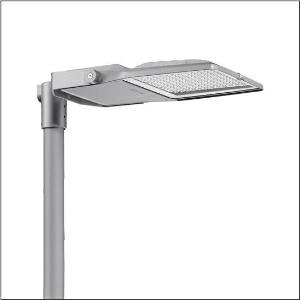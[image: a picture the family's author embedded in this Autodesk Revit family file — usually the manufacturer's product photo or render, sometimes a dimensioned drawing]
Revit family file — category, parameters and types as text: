
# Revit family: floodlight_fl_21_midi___pl64_5xa7785e2e3a_0c5c
name_source: partatom
category: Lighting Fixtures
units: mm (PartAtom-declared; Revit-internal decimal feet)

## family parameters
Cut with Voids When Loaded = No
Host = Face
Light Source = No
Part Type = Normal
Room Calculation Point = No
Round Connector Dimension = Use Diameter
Shared = No

## types (1)
- --- (1 x LED, 26020 lm, 212.4 W, 3000K)
    Apparent Load = 212 VA
    CIE Flux Codes = 28 80 98 100 100
    Color Rendering = 70
    Color Temperature = 3000K
    Default Elevation = 1800 mm
    Description = Floodlight FL 21 midi, floodlight, primary light control with lens, of PMMA, primary optical cover: protective disc, of toughened safety glass, transparent, light distribution: PL64, light emission: direct distribution, installation type: surface-mounted, LED, High Power LED, rated luminous flux: 26.020lm, luminous efficacy: 123lm/W, light colour: 730, colour temperature: 3000K, control gear: ECG Smart Interface, control: flexible luminous flux parameterisation, time-dependent luminous flux control, constant luminous flux control, overheat protection, presetting dimming logarithmic, with terminal, 6-pole, mains connection: 220..240V, AC, 50/60Hz, start of lifetime: 212W, end of service life: 231W, reduction: 95W, luminaire housing, of diecast aluminium, powder-coated, Siteco® metallic grey (DB 702S), sealing non-destructively replaceable, please order mast flange separately, mast bracket, of steel, galvanised, powder-coated, Siteco® metallic grey (DB 702S), Smart Interface above, protection rating (complete): IP66, insulation class (complete): insulation class II (safety insulation), certification: CE, protection symbol: D, impact resistance: IK08, permissible operating ambient temperature: -20..+40°C, permissible operating ambient temperature for outdoor applications: -40..+50°C, standard: DIN EN 12944, LABS conformity tested according to VDMA 24364:2018-05, packaging unit: 1 piece

Light Distribution: PL64
    Height = 76 mm
    Lamp = 1 x LED
    Lamp Light Flux = 26020 lm
    Lamp Power = 212.4 W
    Lamp count = 1
    Length = 657 mm
    Luminous efficacy = 123 lm/W
    Manufacturer = Siteco
    ModVariant = No
    Model = 5XA7785E2E3A
    Number of Poles = 1
    OnlyDefault = Yes
    Power Factor = 1
    Product Name = Floodlight FL 21 midi | PL64
    Product group = floodlight | pylon annexe
    ProductGroupID = 6200
    Protection Class = Protection class II
    Protection Degree = IP 66
    RLX_Detail_Level = 1
    RLX_Emergency_Light_Flux = 0 lm
    RLX_Emergency_Type = 0
    RLX_Emergency_Type_DB = No
    RlxData = <blob elided: 153401 chars, md5=d3fc85f8>
    Socket = socket
    Standby Power = 0 W
    System Light Flux = 26020 lm
    System Power = 212 W
    Type Comments = factory setting: luminous flux: 100 % | dim-lin: 254 | 710 mA
    Type Image = l_1007123.jpg
    URL = http://relux.com
    VarID = @adj_131831
    Voltage = 0 V
    Weight = 0.00 kg
    Width = 442 mm

## geometry (parser evidence)
native form markers: Blend x4, Sweep x14
no freeform markers — native parametric forms only
